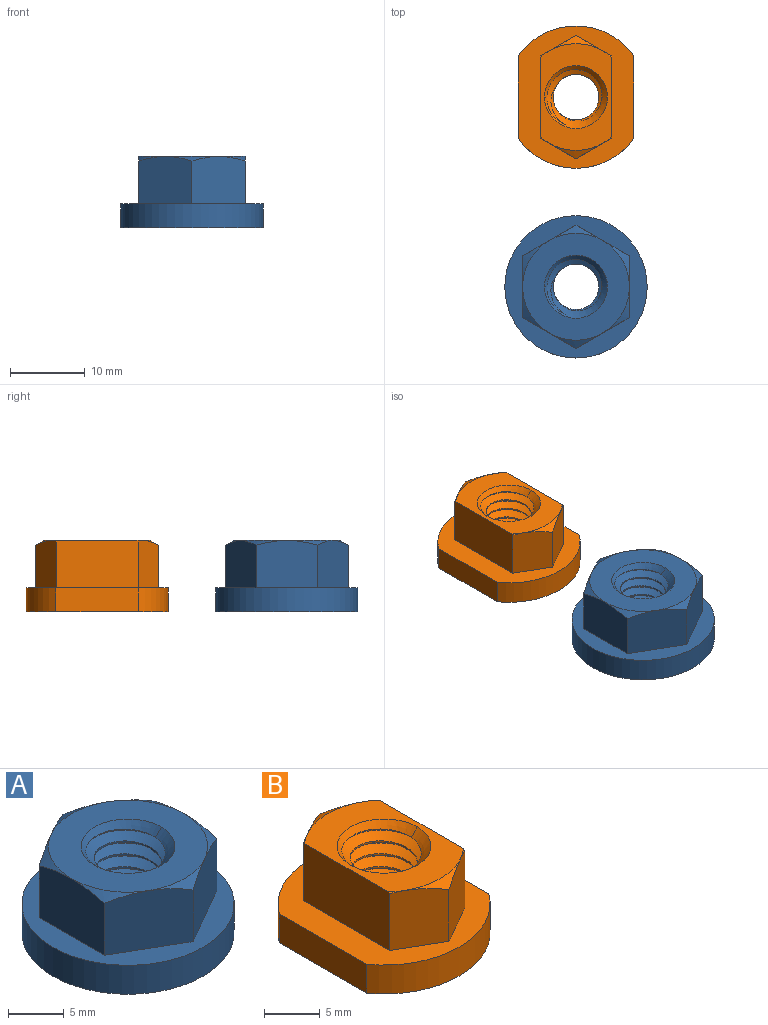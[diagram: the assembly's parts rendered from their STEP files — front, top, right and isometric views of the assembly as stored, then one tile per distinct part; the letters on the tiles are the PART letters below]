
ASSEMBLY  parts=2 mates=1
PART A: 49 faces, bbox 19.7x19.7x10.8 mm
  f0: cone r=0mm half-angle=60deg, axis (0,0,-1), area 5mm2, adj f9,f10,f12
  f1: cone r=0mm half-angle=60deg, axis (0,0,-1), area 5mm2, adj f10,f11,f12
  f2: cone r=0mm half-angle=60deg, axis (0,0,-1), area 5mm2, adj f6,f11,f12
  f3: cone r=0mm half-angle=60deg, axis (0,0,-1), area 5mm2, adj f6,f7,f12
  f4: cone r=0mm half-angle=60deg, axis (0,0,-1), area 5mm2, adj f7,f8,f12
  f5: cone r=0mm half-angle=60deg, axis (0,0,-1), area 5mm2, adj f8,f9,f12
  f6: plane 7.82x7.03mm, normal (-0.5,0.87,0), area 50.6mm2, adj f2,f3,f7,f11,f13
  f7: plane 8.93x7.03mm, normal (-1,0,0), area 50.6mm2, adj f3,f4,f6,f8,f13
  f8: plane 7.82x7.03mm, normal (-0.5,-0.87,0), area 50.6mm2, adj f4,f5,f7,f9,f13
  f9: plane 7.82x7.03mm, normal (0.5,-0.87,0), area 50.6mm2, adj f0,f5,f8,f10,f13
  f10: plane 8.93x7.03mm, normal (1,0,0), area 50.6mm2, adj f0,f1,f9,f11,f13
  f11: plane 7.82x7.03mm, normal (0.5,0.87,0), area 50.6mm2, adj f1,f2,f6,f10,f13
  f12: plane 14.29x14.29mm, normal (0,0,1), area 104.5mm2, adj f0,f1,f2,f3,f4,f5,f14,f17
  f13: plane 19.05x19.05mm, normal (0,0,1), area 108.2mm2, adj f6,f7,f8,f9,f10,f11,f41
  f14: cone r=0mm half-angle=45deg, axis (0,0,1), area 9.4mm2, adj f12,f17,f43
  f15: cylinder r=3.05mm len=0.83mm, axis (0,0,1), area 0mm2, adj f17,f40,f43
  f16: cone r=0mm half-angle=45deg, axis (0,0,1), area 0.3mm2, adj f17,f40,f45
  f17: cone r=0mm half-angle=45deg, axis (0,0,1), area 14.2mm2, adj f12,f14,f15,f16,f18,f43,f45
  f18: cylinder r=3.96mm len=3.72mm, axis (0,0,-1), area 0.6mm2, adj f17,f19,f43,f45
  f19: cylinder r=3.96mm len=7.92mm, axis (0,0,-1), area 2.2mm2, adj f18,f20,f43,f45
  f20: cylinder r=3.96mm len=7.92mm, axis (0,0,-1), area 2.2mm2, adj f19,f21,f43,f45
  f21: cylinder r=3.96mm len=7.92mm, axis (0,0,-1), area 2.2mm2, adj f20,f22,f43,f45
  f22: cylinder r=3.96mm len=7.92mm, axis (0,0,-1), area 2.2mm2, adj f21,f23,f43,f45
  f23: cylinder r=3.96mm len=7.92mm, axis (0,0,-1), area 2.2mm2, adj f22,f24,f43,f45
  f24: cylinder r=3.96mm len=7.92mm, axis (0,0,-1), area 2.2mm2, adj f23,f25,f43,f45
  f25: cylinder r=3.96mm len=7.92mm, axis (0,0,-1), area 2.2mm2, adj f24,f26,f43,f45
  f26: cylinder r=3.96mm len=7.92mm, axis (0,0,-1), area 2.2mm2, adj f25,f27,f43,f45
  f27: cylinder r=3.96mm len=7.92mm, axis (0,0,-1), area 2.2mm2, adj f26,f28,f43,f45
  f28: cylinder r=3.96mm len=7.92mm, axis (0,0,-1), area 2.2mm2, adj f27,f29,f43,f45
  f29: cylinder r=3.96mm len=7.92mm, axis (0,0,-1), area 2.2mm2, adj f28,f30,f43,f45
  f30: cylinder r=3.96mm len=7.92mm, axis (0,0,-1), area 2.2mm2, adj f29,f43,f44,f45
  f31: cylinder r=3.05mm len=6.09mm, axis (0,0,1), area 1.7mm2, adj f32,f42,f43,f45
  f32: cylinder r=3.05mm len=6.09mm, axis (0,0,1), area 1.7mm2, adj f31,f33,f43,f45
  f33: cylinder r=3.05mm len=6.09mm, axis (0,0,1), area 1.7mm2, adj f32,f34,f43,f45
  f34: cylinder r=3.05mm len=6.09mm, axis (0,0,1), area 1.7mm2, adj f33,f35,f43,f45
  f35: cylinder r=3.05mm len=6.09mm, axis (0,0,1), area 1.7mm2, adj f34,f36,f43,f45
  f36: cylinder r=3.05mm len=6.09mm, axis (0,0,1), area 1.7mm2, adj f35,f37,f43,f45
  f37: cylinder r=3.05mm len=6.09mm, axis (0,0,1), area 1.7mm2, adj f36,f38,f43,f45
  f38: cylinder r=3.05mm len=6.09mm, axis (0,0,1), area 1.7mm2, adj f37,f39,f43,f45
  f39: cylinder r=3.05mm len=6.09mm, axis (0,0,1), area 1.7mm2, adj f38,f40,f43,f45
  f40: cylinder r=3.05mm len=6.09mm, axis (0,0,1), area 1.6mm2, adj f15,f16,f39,f43,f45
  f41: cylinder r=9.53mm len=19.05mm, axis (0,0,-1), area 190mm2, adj f13,f46
  f42: cylinder r=3.05mm len=2.67mm, axis (0,0,1), area 0.4mm2, adj f31,f43,f45,f47
  f43: bspline ~9.55x7.91mm, area 134.6mm2, adj f14,f15,f17,f18,f19,f20,f21,f22
  f44: cylinder r=3.96mm len=5.66mm, axis (0,0,-1), area 1.1mm2, adj f30,f43,f45,f47
  f45: bspline ~9.55x7.91mm, area 136.1mm2, adj f16,f17,f18,f19,f20,f21,f22,f23
  f46: plane 19.05x19.05mm, normal (0,0,-1), area 229.2mm2, adj f41,f47,f48
  f47: cone r=0mm half-angle=45deg, axis (0,0,-1), area 12.7mm2, adj f42,f43,f44,f45,f46,f48
  f48: cone r=0mm half-angle=45deg, axis (0,0,-1), area 11.2mm2, adj f45,f46,f47
PART B: 52 faces, bbox 16.2x19.7x10.8 mm
  f0: plane 19.05x15.49mm, normal (0,0,1), area 127.3mm2, adj f1,f7,f8,f9,f10,f41,f48,f49
  f1: cylinder r=9.53mm len=15.49mm, axis (0,0,-1), area 57.5mm2, adj f0,f2,f50,f51
  f2: plane 19.05x15.49mm, normal (0,0,-1), area 202.4mm2, adj f1,f41,f46,f47,f50,f51
  f3: cone r=0mm half-angle=60deg, axis (0,0,-1), area 0.1mm2, adj f9,f11,f48
  f4: cone r=0mm half-angle=60deg, axis (0,0,-1), area 0.1mm2, adj f10,f11,f48
  f5: cone r=0mm half-angle=60deg, axis (0,0,-1), area 0.1mm2, adj f7,f11,f49
  f6: cone r=0mm half-angle=60deg, axis (0,0,-1), area 0.1mm2, adj f8,f11,f49
  f7: plane 7.03x5.44mm, normal (-0.5,0.87,0), area 34mm2, adj f0,f5,f10,f12,f49
  f8: plane 7.03x5.44mm, normal (-0.5,-0.87,0), area 34mm2, adj f0,f6,f9,f13,f49
  f9: plane 7.03x5.44mm, normal (0.5,-0.87,0), area 34mm2, adj f0,f3,f8,f13,f48
  f10: plane 7.03x5.44mm, normal (0.5,0.87,0), area 34mm2, adj f0,f4,f7,f12,f48
  f11: plane 14.29x9.53mm, normal (0,0,1), area 69.3mm2, adj f3,f4,f5,f6,f12,f13,f14,f17
  f12: cone r=0mm half-angle=60deg, axis (0,0,-1), area 5mm2, adj f7,f10,f11
  f13: cone r=0mm half-angle=60deg, axis (0,0,-1), area 5mm2, adj f8,f9,f11
  f14: cone r=0mm half-angle=45deg, axis (0,0,1), area 9.4mm2, adj f11,f17,f43
  f15: cylinder r=3.05mm len=0.83mm, axis (0,0,1), area 0mm2, adj f17,f40,f43
  f16: cone r=0mm half-angle=45deg, axis (0,0,1), area 0.3mm2, adj f17,f40,f45
  f17: cone r=0mm half-angle=45deg, axis (0,0,1), area 14.2mm2, adj f11,f14,f15,f16,f18,f43,f45
  f18: cylinder r=3.96mm len=3.72mm, axis (0,0,-1), area 0.6mm2, adj f17,f19,f43,f45
  f19: cylinder r=3.96mm len=7.92mm, axis (0,0,-1), area 2.2mm2, adj f18,f20,f43,f45
  f20: cylinder r=3.96mm len=7.92mm, axis (0,0,-1), area 2.2mm2, adj f19,f21,f43,f45
  f21: cylinder r=3.96mm len=7.92mm, axis (0,0,-1), area 2.2mm2, adj f20,f22,f43,f45
  f22: cylinder r=3.96mm len=7.92mm, axis (0,0,-1), area 2.2mm2, adj f21,f23,f43,f45
  f23: cylinder r=3.96mm len=7.92mm, axis (0,0,-1), area 2.2mm2, adj f22,f24,f43,f45
  f24: cylinder r=3.96mm len=7.92mm, axis (0,0,-1), area 2.2mm2, adj f23,f25,f43,f45
  f25: cylinder r=3.96mm len=7.92mm, axis (0,0,-1), area 2.2mm2, adj f24,f26,f43,f45
  f26: cylinder r=3.96mm len=7.92mm, axis (0,0,-1), area 2.2mm2, adj f25,f27,f43,f45
  f27: cylinder r=3.96mm len=7.92mm, axis (0,0,-1), area 2.2mm2, adj f26,f28,f43,f45
  f28: cylinder r=3.96mm len=7.92mm, axis (0,0,-1), area 2.2mm2, adj f27,f29,f43,f45
  f29: cylinder r=3.96mm len=7.92mm, axis (0,0,-1), area 2.2mm2, adj f28,f30,f43,f45
  f30: cylinder r=3.96mm len=7.92mm, axis (0,0,-1), area 2.2mm2, adj f29,f43,f44,f45
  f31: cylinder r=3.05mm len=6.09mm, axis (0,0,1), area 1.7mm2, adj f32,f42,f43,f45
  f32: cylinder r=3.05mm len=6.09mm, axis (0,0,1), area 1.7mm2, adj f31,f33,f43,f45
  f33: cylinder r=3.05mm len=6.09mm, axis (0,0,1), area 1.7mm2, adj f32,f34,f43,f45
  f34: cylinder r=3.05mm len=6.09mm, axis (0,0,1), area 1.7mm2, adj f33,f35,f43,f45
  f35: cylinder r=3.05mm len=6.09mm, axis (0,0,1), area 1.7mm2, adj f34,f36,f43,f45
  f36: cylinder r=3.05mm len=6.09mm, axis (0,0,1), area 1.7mm2, adj f35,f37,f43,f45
  f37: cylinder r=3.05mm len=6.09mm, axis (0,0,1), area 1.7mm2, adj f36,f38,f43,f45
  f38: cylinder r=3.05mm len=6.09mm, axis (0,0,1), area 1.7mm2, adj f37,f39,f43,f45
  f39: cylinder r=3.05mm len=6.09mm, axis (0,0,1), area 1.7mm2, adj f38,f40,f43,f45
  f40: cylinder r=3.05mm len=6.09mm, axis (0,0,1), area 1.6mm2, adj f15,f16,f39,f43,f45
  f41: cylinder r=9.53mm len=15.49mm, axis (0,0,-1), area 57.5mm2, adj f0,f2,f50,f51
  f42: cylinder r=3.05mm len=2.67mm, axis (0,0,1), area 0.4mm2, adj f31,f43,f45,f46
  f43: bspline ~9.55x7.91mm, area 134.6mm2, adj f14,f15,f17,f18,f19,f20,f21,f22
  f44: cylinder r=3.96mm len=5.66mm, axis (0,0,-1), area 1.1mm2, adj f30,f43,f45,f46
  f45: bspline ~9.55x7.91mm, area 136.1mm2, adj f16,f17,f18,f19,f20,f21,f22,f23
  f46: cone r=0mm half-angle=45deg, axis (0,0,-1), area 12.7mm2, adj f2,f42,f43,f44,f45,f47
  f47: cone r=0mm half-angle=45deg, axis (0,0,-1), area 11.2mm2, adj f2,f45,f46
  f48: plane 11x6.35mm, normal (1,0,0), area 69.8mm2, adj f0,f3,f4,f9,f10,f11
  f49: plane 11x6.35mm, normal (-1,0,0), area 69.8mm2, adj f0,f5,f6,f7,f8,f11
  f50: plane 11.08x3.18mm, normal (1,0,0), area 35.2mm2, adj f0,f1,f2,f41
  f51: plane 11.08x3.18mm, normal (-1,0,0), area 35.2mm2, adj f0,f1,f2,f41
PLACE A t=(0,-25.4,0)mm
PLACE B at identity
MATE fastened A.f0 <-> B.f2  axis (0,0,-1) through (0,-25.4,-9.52)mm
